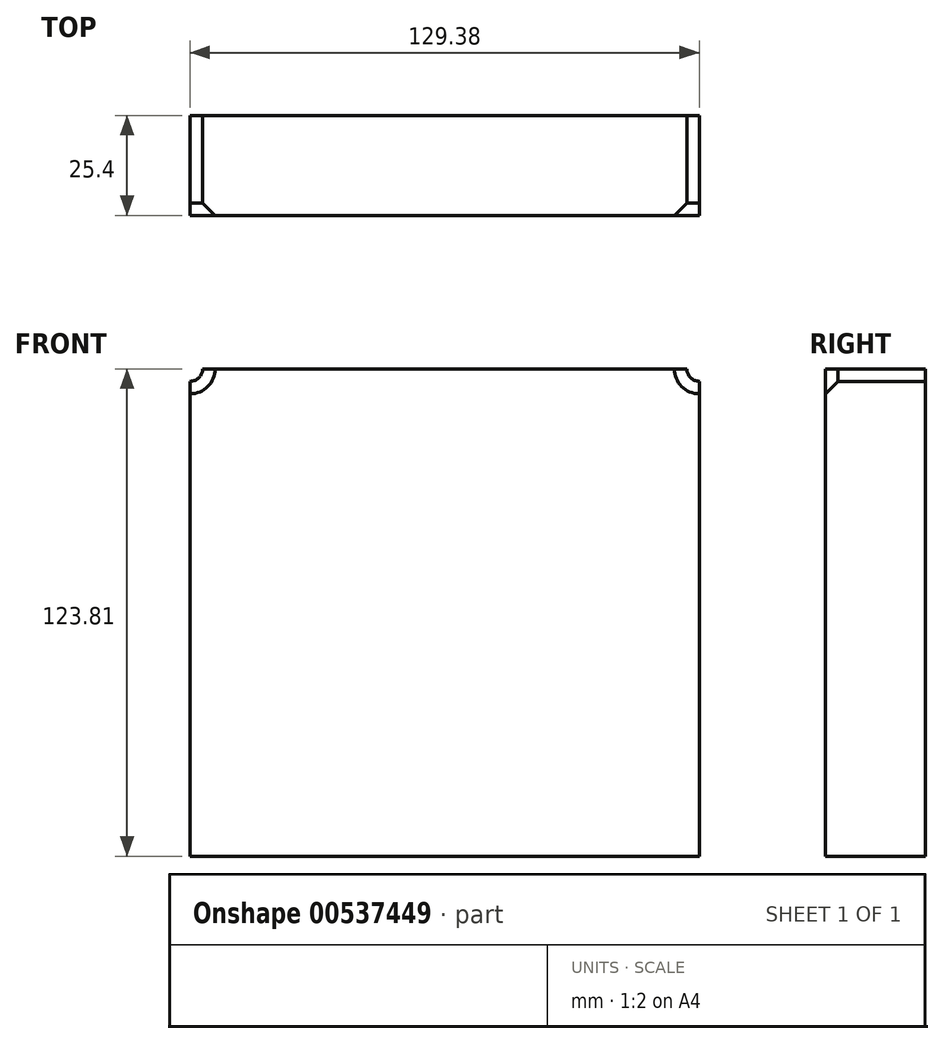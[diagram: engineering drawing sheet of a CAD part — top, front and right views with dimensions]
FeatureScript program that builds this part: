
annotation { "Feature Type Name" : "Feature", "Feature Type Description" : "" }
export const myFeature = defineFeature(function(context is Context, id is Id, definition is map)
    precondition{}
    {
        {
            var Q0;
            Q0=qCreatedBy(makeId("Front.planeOp"),FACE);
            var sketch = newSketch(context, id + "F0", { "sketchPlane" : qUnion([Q0])});
            skLineSegment(sketch, "E0.bottom", {"start": v(-64.7, 59.97) * mm, "end": v(64.67, 59.97) * mm});
            skLineSegment(sketch, "E0.top", {"start": v(-64.7, -63.84) * mm, "end": v(64.67, -63.84) * mm});
            skLineSegment(sketch, "E0.left", {"start": v(-64.7, 59.97) * mm, "end": v(-64.7, -63.84) * mm});
            skLineSegment(sketch, "E0.right", {"start": v(64.67, 59.97) * mm, "end": v(64.67, -63.84) * mm});
            skSolve(sketch);
        }
        {
            var Q0;
            Q0=makeQuery(id+"F0.imprint","IMPRINT",FACE,{"disambiguationData":[TD([[makeQuery(id+"F0.imprint","IMPRINT",EDGE,{"derivedFrom":sQuery(id+"F0.wireOp",EDGE,"E0.bottom")}),-1.0]])]});
            var sketch = newSketch(context, id + "F1", { "sketchPlane" : qUnion([Q0])});
            skSolve(sketch);
        }
        {
            var Q0;
            Q0=makeQuery(id+"F1.imprint","IMPRINT",FACE,{"disambiguationData":[TD([[makeQuery(id+"F1.imprint","IMPRINT",EDGE,{"derivedFrom":makeQuery(id+"F0.imprint","IMPRINT",EDGE,{"derivedFrom":sQuery(id+"F0.wireOp",EDGE,"E0.bottom")})}),-1.0]])]});
            extrude(context, id + "F2", {"entities" : qUnion([Q0]), "oppositeDirection" : true, "depth" : 25.4 * mm, "offsetDistance" : 25.4 * mm});
        }
        {
            var Q0;
            Q0=sQuery(id+"F0.wireOp",VERTEX,"E0.bottom.end");
            var Q1;
            Q1=sQuery(id+"F0.wireOp",VERTEX,"E0.left.start");
            var Q2;
            Q2=makeQuery(id+"F2.opExtrude","SWEPT_BODY",BODY,{"disambiguationData":[OSD([sQuery(id+"F0.wireOp",EDGE,"E0.bottom"),sQuery(id+"F0.wireOp",EDGE,"E0.top"),sQuery(id+"F0.wireOp",EDGE,"E0.left"),sQuery(id+"F0.wireOp",EDGE,"E0.right")])]});
            hole(context, id + "F3", {"style" : HoleStyle.C_SINK, "endStyle" : HoleEndStyle.THROUGH, "holeDiameter" : 6.35 * mm, "cSinkDiameter" : 12.7 * mm, "cSinkAngle" : 90 * degree, "isTappedThrough" : true, "tappedDepth" : 12.7 * mm, "tapClearance" : 3, "locations" : qUnion([Q0, Q1]), "scope" : qUnion([Q2])});
        }
    });
